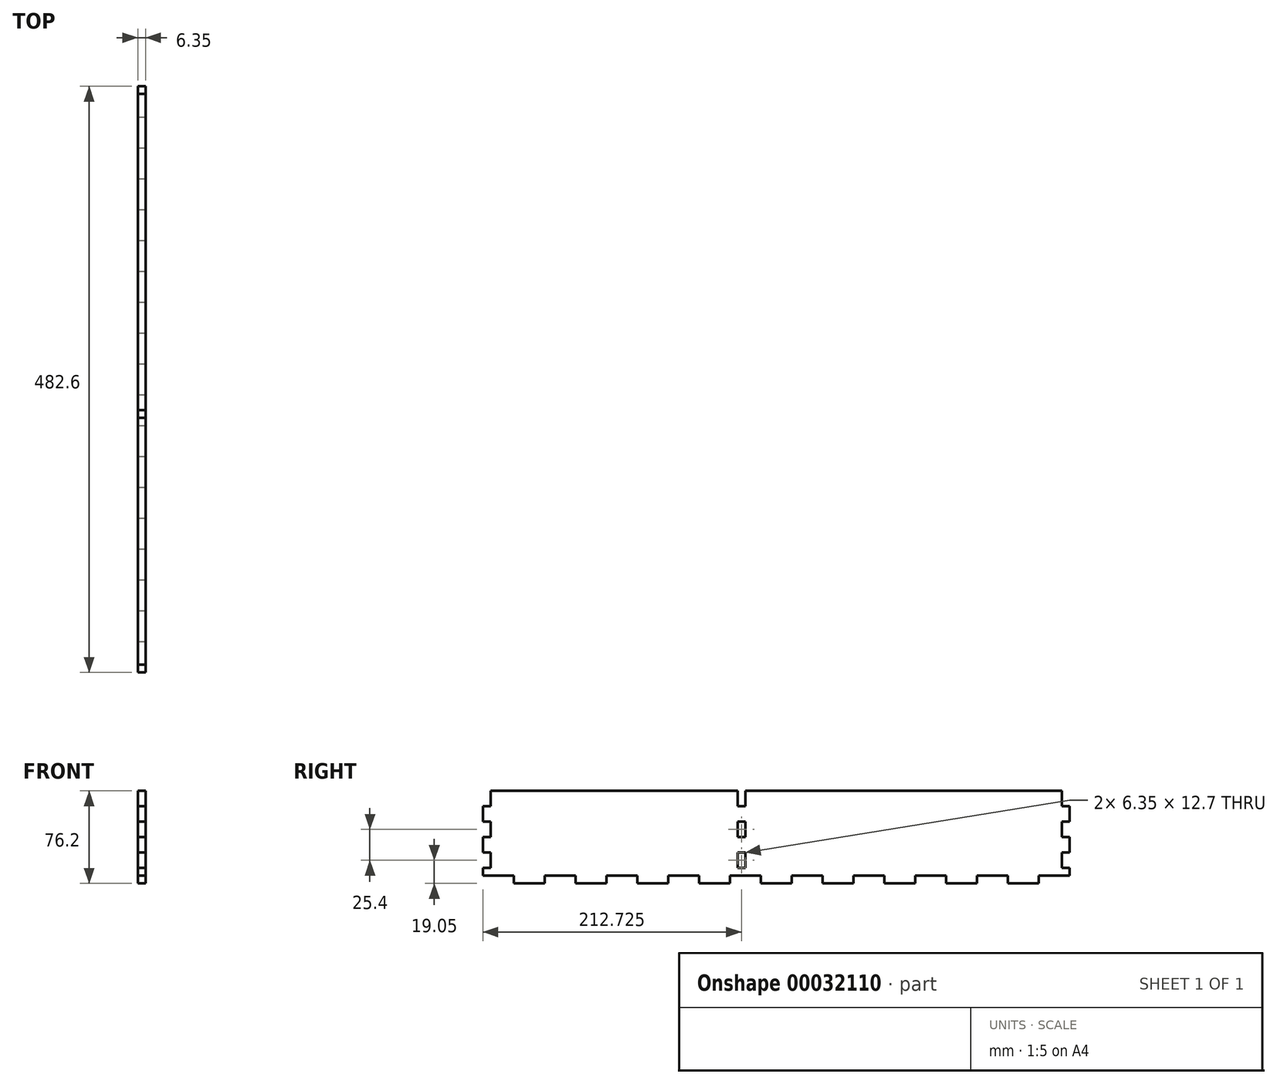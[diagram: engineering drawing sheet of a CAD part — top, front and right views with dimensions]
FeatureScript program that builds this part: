
annotation { "Feature Type Name" : "Feature", "Feature Type Description" : "" }
export const myFeature = defineFeature(function(context is Context, id is Id, definition is map)
    precondition{}
    {
        {
            var Q0;
            Q0=qCreatedBy(makeId("Right.planeOp"),FACE);
            var sketch = newSketch(context, id + "F0", { "sketchPlane" : qUnion([Q0])});
            skLineSegment(sketch, "E0.rect.bottom", {"start": v(-241.3, 38.1) * mm, "end": v(241.3, 38.1) * mm});
            skLineSegment(sketch, "E0.rect.top", {"start": v(-241.3, -38.1) * mm, "end": v(241.3, -38.1) * mm});
            skLineSegment(sketch, "E0.rect.left", {"start": v(-241.3, 38.1) * mm, "end": v(-241.3, -38.1) * mm});
            skLineSegment(sketch, "E0.rect.right", {"start": v(241.3, 38.1) * mm, "end": v(241.3, -38.1) * mm});
            skPoint(sketch, "E0.rect.middle", {"position": v(0, 0) * mm});
            skSolve(sketch);
        }
        {
            var Q0;
            Q0=makeQuery(id+"F0.imprint","IMPRINT",FACE,{"disambiguationData":[TD([[makeQuery(id+"F0.imprint","IMPRINT",EDGE,{"derivedFrom":sQuery(id+"F0.wireOp",EDGE,"E0.rect.bottom")}),-1.0]])]});
            extrude(context, id + "F1", {"entities" : qUnion([Q0]), "depth" : 6.35 * mm});
        }
        {
            var Q0;
            Q0=makeQuery(id+"F1.opExtrude","CAP_FACE",FACE,{"disambiguationData":[OSD([sQuery(id+"F0.wireOp",EDGE,"E0.rect.bottom"),sQuery(id+"F0.wireOp",EDGE,"E0.rect.top"),sQuery(id+"F0.wireOp",EDGE,"E0.rect.left"),sQuery(id+"F0.wireOp",EDGE,"E0.rect.right")])],"isStart":false});
            var sketch = newSketch(context, id + "F2", { "sketchPlane" : qUnion([Q0])});
            skLineSegment(sketch, "E1.bottom", {"start": v(-241.3, -38.1) * mm, "end": v(-215.9, -38.1) * mm});
            skLineSegment(sketch, "E1.top", {"start": v(-241.3, -31.75) * mm, "end": v(-215.9, -31.75) * mm});
            skLineSegment(sketch, "E1.left", {"start": v(-241.3, -38.1) * mm, "end": v(-241.3, -31.75) * mm});
            skLineSegment(sketch, "E1.right", {"start": v(-215.9, -38.1) * mm, "end": v(-215.9, -31.75) * mm});
            skLineSegment(sketch, "E2.1.0.0", {"start": v(-190.5, -38.1) * mm, "end": v(-165.1, -38.1) * mm});
            skLineSegment(sketch, "E2.1.0.1", {"start": v(-190.5, -31.75) * mm, "end": v(-165.1, -31.75) * mm});
            skLineSegment(sketch, "E2.1.0.2", {"start": v(-190.5, -38.1) * mm, "end": v(-190.5, -31.75) * mm});
            skLineSegment(sketch, "E2.1.0.3", {"start": v(-165.1, -38.1) * mm, "end": v(-165.1, -31.75) * mm});
            skLineSegment(sketch, "E2.2.0.0", {"start": v(-139.7, -38.1) * mm, "end": v(-114.3, -38.1) * mm});
            skLineSegment(sketch, "E2.2.0.1", {"start": v(-139.7, -31.75) * mm, "end": v(-114.3, -31.75) * mm});
            skLineSegment(sketch, "E2.2.0.2", {"start": v(-139.7, -38.1) * mm, "end": v(-139.7, -31.75) * mm});
            skLineSegment(sketch, "E2.2.0.3", {"start": v(-114.3, -38.1) * mm, "end": v(-114.3, -31.75) * mm});
            skLineSegment(sketch, "E2.3.0.0", {"start": v(-88.9, -38.1) * mm, "end": v(-63.5, -38.1) * mm});
            skLineSegment(sketch, "E2.3.0.1", {"start": v(-88.9, -31.75) * mm, "end": v(-63.5, -31.75) * mm});
            skLineSegment(sketch, "E2.3.0.2", {"start": v(-88.9, -38.1) * mm, "end": v(-88.9, -31.75) * mm});
            skLineSegment(sketch, "E2.3.0.3", {"start": v(-63.5, -38.1) * mm, "end": v(-63.5, -31.75) * mm});
            skLineSegment(sketch, "E2.4.0.0", {"start": v(-38.1, -38.1) * mm, "end": v(-12.7, -38.1) * mm});
            skLineSegment(sketch, "E2.4.0.1", {"start": v(-38.1, -31.75) * mm, "end": v(-12.7, -31.75) * mm});
            skLineSegment(sketch, "E2.4.0.2", {"start": v(-38.1, -38.1) * mm, "end": v(-38.1, -31.75) * mm});
            skLineSegment(sketch, "E2.4.0.3", {"start": v(-12.7, -38.1) * mm, "end": v(-12.7, -31.75) * mm});
            skLineSegment(sketch, "E2.5.0.0", {"start": v(12.7, -38.1) * mm, "end": v(38.1, -38.1) * mm});
            skLineSegment(sketch, "E2.5.0.1", {"start": v(12.7, -31.75) * mm, "end": v(38.1, -31.75) * mm});
            skLineSegment(sketch, "E2.5.0.2", {"start": v(12.7, -38.1) * mm, "end": v(12.7, -31.75) * mm});
            skLineSegment(sketch, "E2.5.0.3", {"start": v(38.1, -38.1) * mm, "end": v(38.1, -31.75) * mm});
            skLineSegment(sketch, "E2.6.0.0", {"start": v(63.5, -38.1) * mm, "end": v(88.9, -38.1) * mm});
            skLineSegment(sketch, "E2.6.0.1", {"start": v(63.5, -31.75) * mm, "end": v(88.9, -31.75) * mm});
            skLineSegment(sketch, "E2.6.0.2", {"start": v(63.5, -38.1) * mm, "end": v(63.5, -31.75) * mm});
            skLineSegment(sketch, "E2.6.0.3", {"start": v(88.9, -38.1) * mm, "end": v(88.9, -31.75) * mm});
            skLineSegment(sketch, "E2.7.0.0", {"start": v(114.3, -38.1) * mm, "end": v(139.7, -38.1) * mm});
            skLineSegment(sketch, "E2.7.0.1", {"start": v(114.3, -31.75) * mm, "end": v(139.7, -31.75) * mm});
            skLineSegment(sketch, "E2.7.0.2", {"start": v(114.3, -38.1) * mm, "end": v(114.3, -31.75) * mm});
            skLineSegment(sketch, "E2.7.0.3", {"start": v(139.7, -38.1) * mm, "end": v(139.7, -31.75) * mm});
            skLineSegment(sketch, "E2.8.0.0", {"start": v(165.1, -38.1) * mm, "end": v(190.5, -38.1) * mm});
            skLineSegment(sketch, "E2.8.0.1", {"start": v(165.1, -31.75) * mm, "end": v(190.5, -31.75) * mm});
            skLineSegment(sketch, "E2.8.0.2", {"start": v(165.1, -38.1) * mm, "end": v(165.1, -31.75) * mm});
            skLineSegment(sketch, "E2.8.0.3", {"start": v(190.5, -38.1) * mm, "end": v(190.5, -31.75) * mm});
            skLineSegment(sketch, "E2.9.0.0", {"start": v(215.9, -38.1) * mm, "end": v(241.3, -38.1) * mm});
            skLineSegment(sketch, "E2.9.0.1", {"start": v(215.9, -31.75) * mm, "end": v(241.3, -31.75) * mm});
            skLineSegment(sketch, "E2.9.0.2", {"start": v(215.9, -38.1) * mm, "end": v(215.9, -31.75) * mm});
            skLineSegment(sketch, "E2.9.0.3", {"start": v(241.3, -38.1) * mm, "end": v(241.3, -31.75) * mm});
            skLineSegment(sketch, "E2.direction1", {"start": v(-241.3, -38.1) * mm, "end": v(-190.5, -38.1) * mm, "construction": true});
            skSolve(sketch);
        }
        {
            var Q0;
            Q0 = qSketchRegion(id + "F2", true);
            extrude(context, id + "F3", {"entities" : qUnion([Q0]), "operationType" : NewBodyOperationType.REMOVE, "endBound" : BoundingType.UP_TO_NEXT, "oppositeDirection" : true, "depth" : 25.4 * mm});
        }
        {
            var Q0;
            Q0=makeQuery(id+"F1.opExtrude","CAP_FACE",FACE,{"disambiguationData":[OSD([sQuery(id+"F0.wireOp",EDGE,"E0.rect.bottom"),sQuery(id+"F0.wireOp",EDGE,"E0.rect.top"),sQuery(id+"F0.wireOp",EDGE,"E0.rect.left"),sQuery(id+"F0.wireOp",EDGE,"E0.rect.right")])],"isStart":false});
            var sketch = newSketch(context, id + "F4", { "sketchPlane" : qUnion([Q0])});
            skLineSegment(sketch, "E3.bottom", {"start": v(-241.3, 38.1) * mm, "end": v(-234.95, 38.1) * mm});
            skLineSegment(sketch, "E3.top", {"start": v(-241.3, 25.4) * mm, "end": v(-234.95, 25.4) * mm});
            skLineSegment(sketch, "E3.left", {"start": v(-241.3, 38.1) * mm, "end": v(-241.3, 25.4) * mm});
            skLineSegment(sketch, "E3.right", {"start": v(-234.95, 38.1) * mm, "end": v(-234.95, 25.4) * mm});
            skLineSegment(sketch, "E4", {"start": v(0, 38.1) * mm, "end": v(0, -38.1) * mm, "construction": true});
            skLineSegment(sketch, "E5.0.1.0", {"start": v(-241.3, 12.7) * mm, "end": v(-241.3, 0) * mm});
            skLineSegment(sketch, "E5.0.1.1", {"start": v(-241.3, 12.7) * mm, "end": v(-234.95, 12.7) * mm});
            skLineSegment(sketch, "E5.0.1.2", {"start": v(-241.3, 0) * mm, "end": v(-234.95, 0) * mm});
            skLineSegment(sketch, "E5.0.1.3", {"start": v(-234.95, 12.7) * mm, "end": v(-234.95, 0) * mm});
            skLineSegment(sketch, "E5.0.2.0", {"start": v(-241.3, -12.7) * mm, "end": v(-241.3, -25.4) * mm});
            skLineSegment(sketch, "E5.0.2.1", {"start": v(-241.3, -12.7) * mm, "end": v(-234.95, -12.7) * mm});
            skLineSegment(sketch, "E5.0.2.2", {"start": v(-241.3, -25.4) * mm, "end": v(-234.95, -25.4) * mm});
            skLineSegment(sketch, "E5.0.2.3", {"start": v(-234.95, -12.7) * mm, "end": v(-234.95, -25.4) * mm});
            skLineSegment(sketch, "E5.1.0.0", {"start": v(-31.75, 38.1) * mm, "end": v(-31.75, 25.4) * mm});
            skLineSegment(sketch, "E5.1.0.1", {"start": v(-31.75, 38.1) * mm, "end": v(-25.4, 38.1) * mm});
            skLineSegment(sketch, "E5.1.0.2", {"start": v(-31.75, 25.4) * mm, "end": v(-25.4, 25.4) * mm});
            skLineSegment(sketch, "E5.1.0.3", {"start": v(-25.4, 38.1) * mm, "end": v(-25.4, 25.4) * mm});
            skLineSegment(sketch, "E5.1.1.0", {"start": v(-31.75, 12.7) * mm, "end": v(-31.75, 0) * mm});
            skLineSegment(sketch, "E5.1.1.1", {"start": v(-31.75, 12.7) * mm, "end": v(-25.4, 12.7) * mm});
            skLineSegment(sketch, "E5.1.1.2", {"start": v(-31.75, 0) * mm, "end": v(-25.4, 0) * mm});
            skLineSegment(sketch, "E5.1.1.3", {"start": v(-25.4, 12.7) * mm, "end": v(-25.4, 0) * mm});
            skLineSegment(sketch, "E5.1.2.0", {"start": v(-31.75, -12.7) * mm, "end": v(-31.75, -25.4) * mm});
            skLineSegment(sketch, "E5.1.2.1", {"start": v(-31.75, -12.7) * mm, "end": v(-25.4, -12.7) * mm});
            skLineSegment(sketch, "E5.1.2.2", {"start": v(-31.75, -25.4) * mm, "end": v(-25.4, -25.4) * mm});
            skLineSegment(sketch, "E5.1.2.3", {"start": v(-25.4, -12.7) * mm, "end": v(-25.4, -25.4) * mm});
            skLineSegment(sketch, "E5.direction1", {"start": v(-241.3, 25.4) * mm, "end": v(-31.75, 25.4) * mm, "construction": true});
            skLineSegment(sketch, "E5.direction2", {"start": v(-241.3, 25.4) * mm, "end": v(-241.3, 0) * mm, "construction": true});
            skLineSegment(sketch, "E6.MirrorCS", {"start": v(241.3, 38.1) * mm, "end": v(241.3, 25.4) * mm});
            skLineSegment(sketch, "E7.MirrorCS", {"start": v(241.3, 38.1) * mm, "end": v(234.95, 38.1) * mm});
            skLineSegment(sketch, "E8.MirrorCS", {"start": v(234.95, 38.1) * mm, "end": v(234.95, 25.4) * mm});
            skLineSegment(sketch, "E9.MirrorCS", {"start": v(241.3, 25.4) * mm, "end": v(234.95, 25.4) * mm});
            skLineSegment(sketch, "E10.MirrorCS", {"start": v(241.3, 12.7) * mm, "end": v(234.95, 12.7) * mm});
            skLineSegment(sketch, "E11.MirrorCS", {"start": v(241.3, 12.7) * mm, "end": v(241.3, 0) * mm});
            skLineSegment(sketch, "E12.MirrorCS", {"start": v(241.3, 0) * mm, "end": v(234.95, 0) * mm});
            skLineSegment(sketch, "E13.MirrorCS", {"start": v(234.95, 12.7) * mm, "end": v(234.95, 0) * mm});
            skLineSegment(sketch, "E14.MirrorCS", {"start": v(241.3, -12.7) * mm, "end": v(234.95, -12.7) * mm});
            skLineSegment(sketch, "E15.MirrorCS", {"start": v(241.3, -12.7) * mm, "end": v(241.3, -25.4) * mm});
            skLineSegment(sketch, "E16.MirrorCS", {"start": v(241.3, -25.4) * mm, "end": v(234.95, -25.4) * mm});
            skLineSegment(sketch, "E17.MirrorCS", {"start": v(234.95, -12.7) * mm, "end": v(234.95, -25.4) * mm});
            skSolve(sketch);
        }
        {
            var Q0;
            Q0 = qSketchRegion(id + "F4", true);
            extrude(context, id + "F5", {"entities" : qUnion([Q0]), "operationType" : NewBodyOperationType.REMOVE, "endBound" : BoundingType.UP_TO_NEXT, "oppositeDirection" : true, "depth" : 6.35 * mm});
        }
    });
